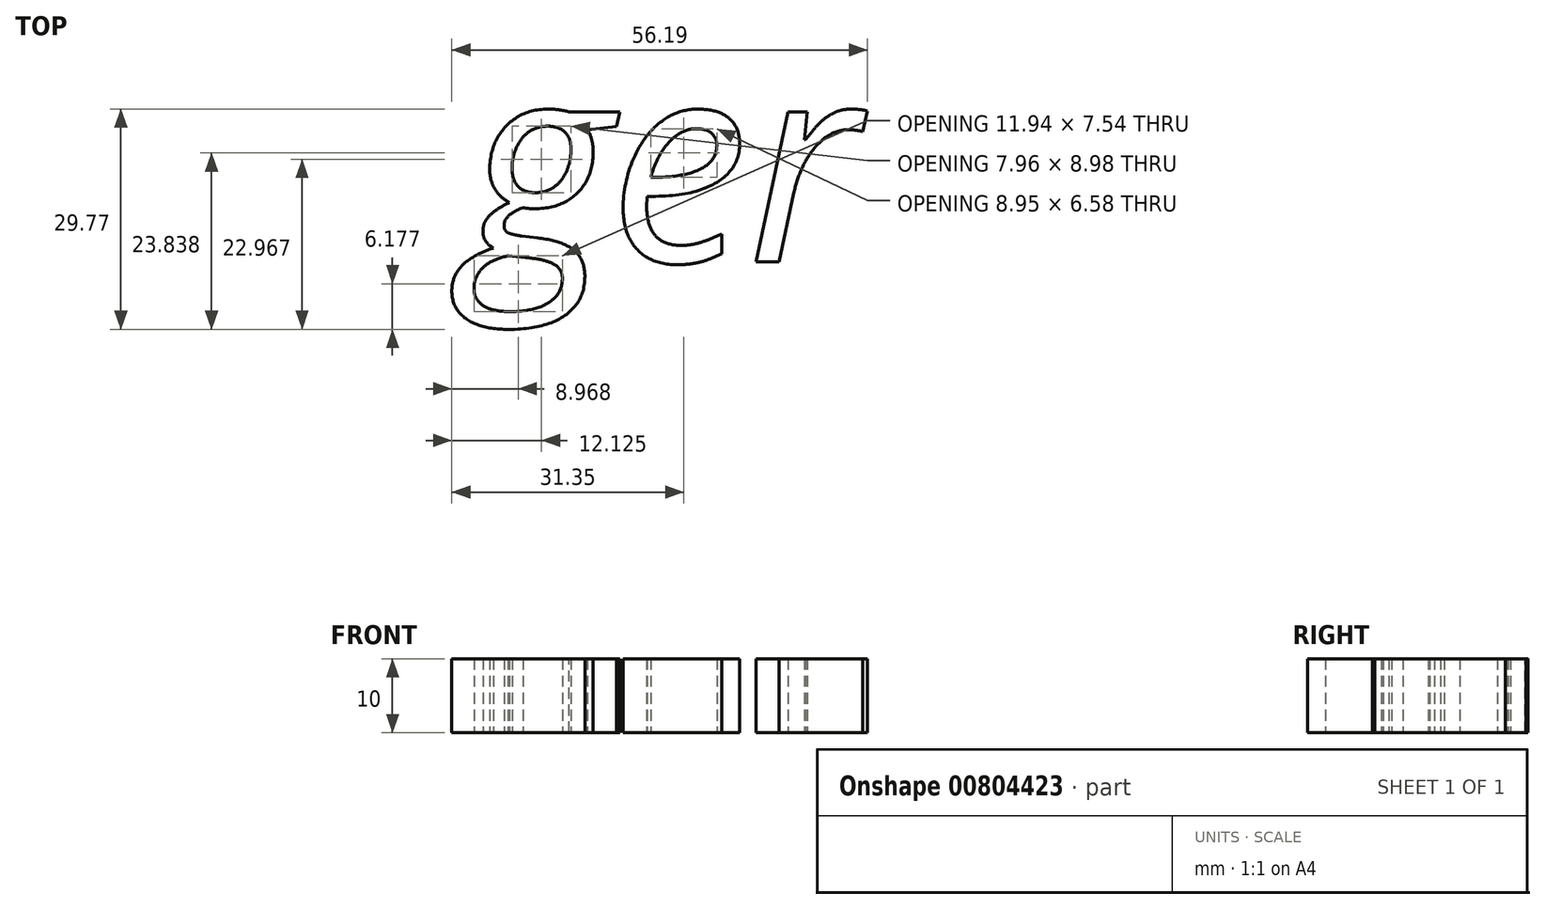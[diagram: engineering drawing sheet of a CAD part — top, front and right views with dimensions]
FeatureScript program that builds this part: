
annotation { "Feature Type Name" : "Feature", "Feature Type Description" : "" }
export const myFeature = defineFeature(function(context is Context, id is Id, definition is map)
    precondition{}
    {
        {
            var Q0;
            Q0=qCreatedBy(makeId("Top.planeOp"),FACE);
            var sketch = newSketch(context, id + "F0", { "sketchPlane" : qUnion([Q0])});
            skText(sketch, "E0", { "text": "ger", "fontName": "OpenSans-Italic.ttf"});
            const initialGuessF0  = {"E0": [0.00618, 0.01538, 1, 0, 0.0273]};
            skSetInitialGuess(sketch, initialGuessF0);
            skSolve(sketch);
        }
        {
            var Q0;
            Q0 = qSketchRegion(id + "F0", true);
            extrude(context, id + "F1", {"entities" : qUnion([Q0]), "depth" : 10 * mm, "offsetDistance" : 25 * mm});
        }
    });
